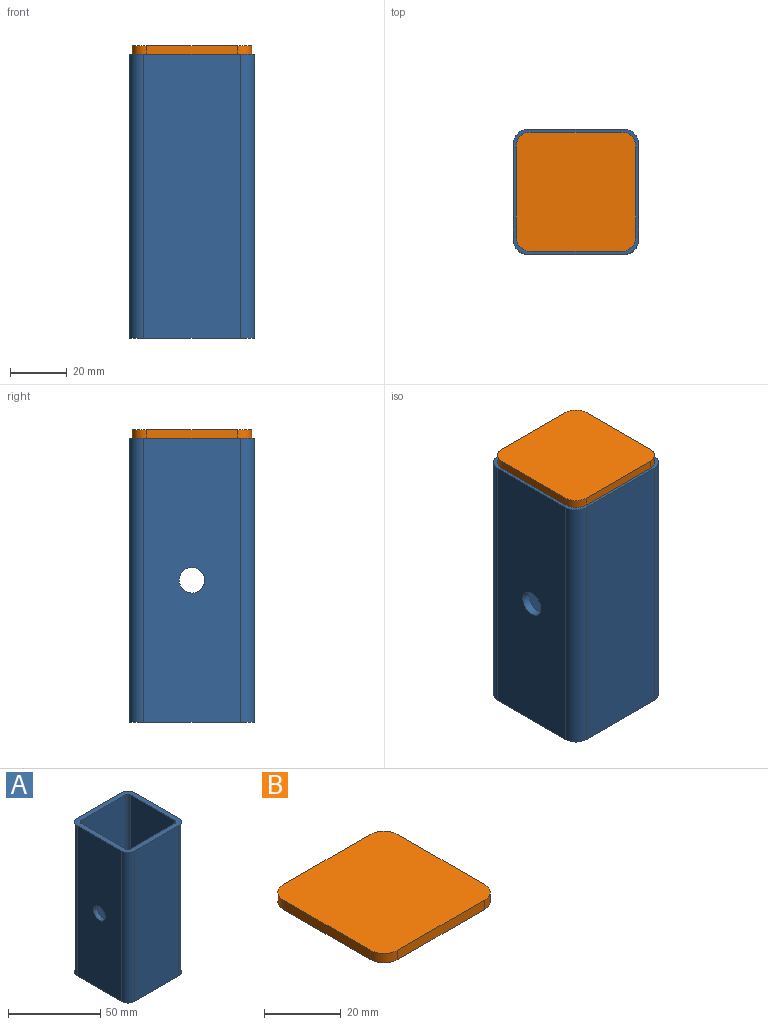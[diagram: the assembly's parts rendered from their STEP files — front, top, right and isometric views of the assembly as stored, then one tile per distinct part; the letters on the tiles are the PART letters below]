
ASSEMBLY  parts=2 mates=1
PART A: 20 faces, bbox 44x44x100 mm
  f0: plane 100x34mm, normal (0,-1,0), area 3400mm2, adj f1,f7,f8,f9
  f1: cylinder r=5mm len=100mm, axis (0,0,-1), area 785.4mm2, adj f0,f2,f8,f9
  f2: plane 100x34mm, normal (1,0,0), area 3336.4mm2, adj f1,f3,f8,f9,f18
  f3: cylinder r=5mm len=100mm, axis (0,0,-1), area 785.4mm2, adj f2,f4,f8,f9
  f4: plane 100x34mm, normal (0,1,0), area 3400mm2, adj f3,f5,f8,f9
  f5: cylinder r=5mm len=100mm, axis (0,0,-1), area 785.4mm2, adj f4,f6,f8,f9
  f6: plane 100x34mm, normal (-1,0,0), area 3336.4mm2, adj f5,f7,f8,f9,f19
  f7: cylinder r=5mm len=100mm, axis (0,0,-1), area 785.4mm2, adj f0,f6,f8,f9
  f8: plane 44x44mm, normal (0,0,1), area 474mm2, adj f0,f1,f2,f3,f4,f5,f6,f7
  f9: plane 44x44mm, normal (0,0,-1), area 474mm2, adj f0,f1,f2,f3,f4,f5,f6,f7
  f10: cylinder r=2mm len=100mm, axis (0,0,1), area 314.2mm2, adj f8,f9,f11,f17
  f11: plane 100x34mm, normal (0,-1,0), area 3400mm2, adj f8,f9,f10,f12
  f12: cylinder r=2mm len=100mm, axis (0,0,1), area 314.2mm2, adj f8,f9,f11,f13
  f13: plane 100x34mm, normal (1,0,0), area 3336.4mm2, adj f8,f9,f12,f14,f19
  f14: cylinder r=2mm len=100mm, axis (0,0,1), area 314.2mm2, adj f8,f9,f13,f15
  f15: plane 100x34mm, normal (0,1,0), area 3400mm2, adj f8,f9,f14,f16
  f16: cylinder r=2mm len=100mm, axis (0,0,1), area 314.2mm2, adj f8,f9,f15,f17
  f17: plane 100x34mm, normal (-1,0,0), area 3336.4mm2, adj f8,f9,f10,f16,f18
  f18: cylinder r=4.5mm len=9mm, axis (1,0,0), area 84.8mm2, adj f2,f17
  f19: cylinder r=4.5mm len=9mm, axis (1,0,0), area 84.8mm2, adj f6,f13
PART B: 10 faces, bbox 42x42x3 mm
  f0: plane 32x3mm, normal (0,-1,0), area 96mm2, adj f4,f5,f6,f9
  f1: plane 32x3mm, normal (1,0,0), area 96mm2, adj f4,f5,f6,f7
  f2: plane 32x3mm, normal (0,1,0), area 96mm2, adj f4,f5,f7,f8
  f3: plane 32x3mm, normal (-1,0,0), area 96mm2, adj f4,f5,f8,f9
  f4: plane 42x42mm, normal (0,0,1), area 1742.5mm2, adj f0,f1,f2,f3,f6,f7,f8,f9
  f5: plane 42x42mm, normal (0,0,-1), area 1742.5mm2, adj f0,f1,f2,f3,f6,f7,f8,f9
  f6: cylinder r=5mm len=5mm, axis (0,0,-1), area 23.6mm2, adj f0,f1,f4,f5
  f7: cylinder r=5mm len=5mm, axis (0,0,1), area 23.6mm2, adj f1,f2,f4,f5
  f8: cylinder r=5mm len=5mm, axis (0,0,-1), area 23.6mm2, adj f2,f3,f4,f5
  f9: cylinder r=5mm len=5mm, axis (0,0,1), area 23.6mm2, adj f0,f3,f4,f5
PLACE A t=(6.31,-52.7,-331.51)mm fixed
PLACE B t=(6.31,-52.7,-231.51)mm
MATE fastened B.f5 <-> A.f8  axis (0,0,-1) through (6.31,-52.7,-231.51)mm
